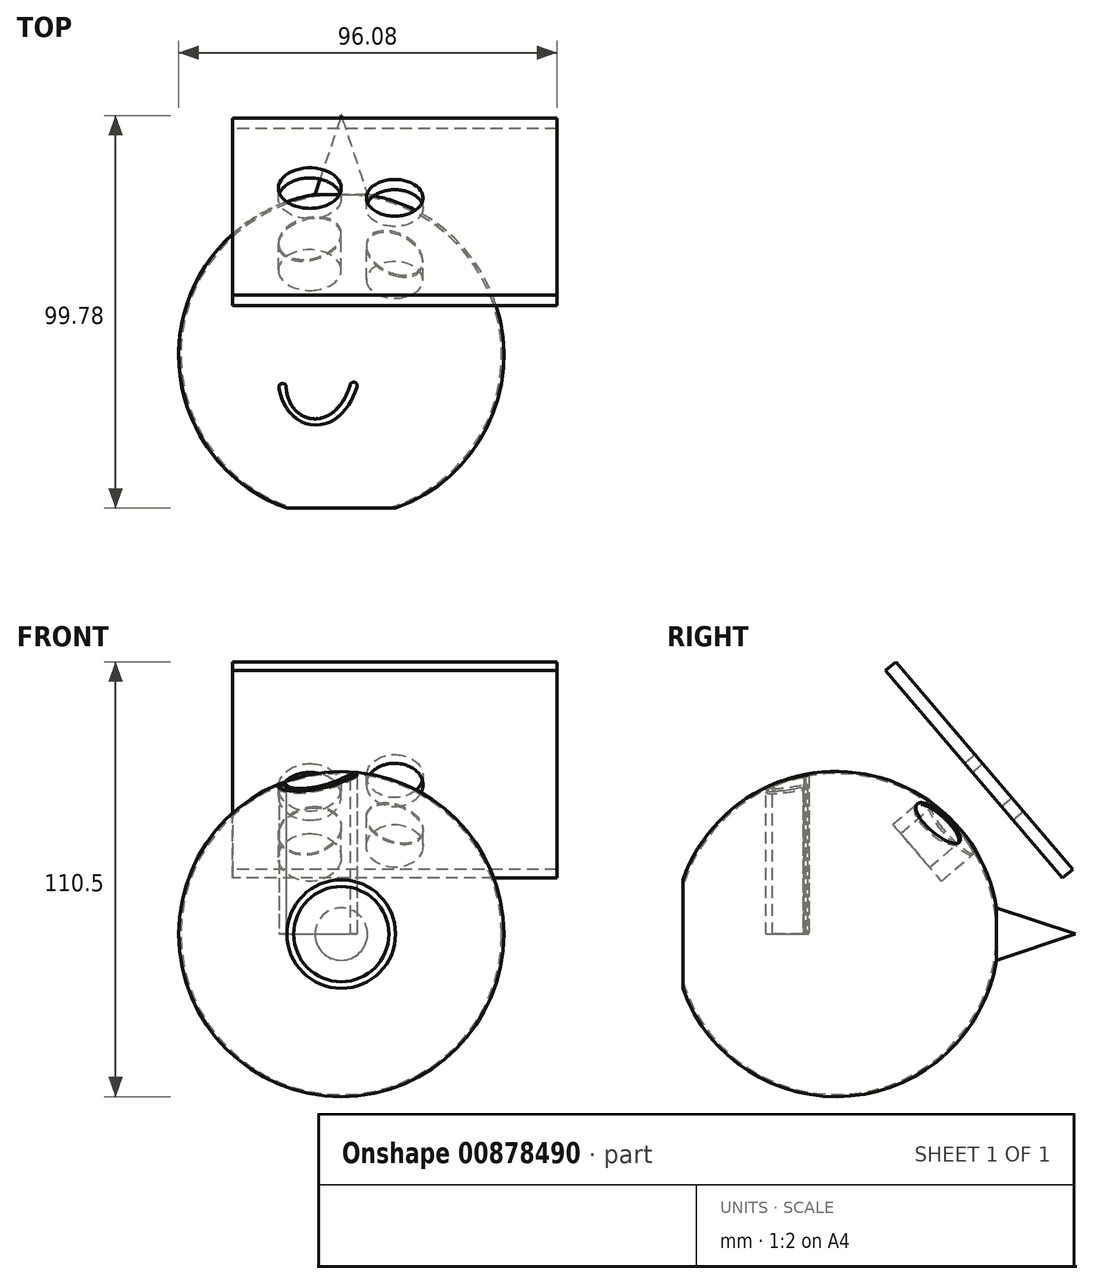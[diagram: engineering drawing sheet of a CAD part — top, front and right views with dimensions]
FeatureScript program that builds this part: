
annotation { "Feature Type Name" : "Feature", "Feature Type Description" : "" }
export const myFeature = defineFeature(function(context is Context, id is Id, definition is map)
    precondition{}
    {
        {
            var Q0;
            Q0=qCreatedBy(makeId("Top.planeOp"),FACE);
            var sketch = newSketch(context, id + "F0", { "sketchPlane" : qUnion([Q0])});
            skLineSegment(sketch, "E0.bottom", {"start": v(-58.97, 67.37) * mm, "end": v(80.08, 67.37) * mm});
            skLineSegment(sketch, "E0.top", {"start": v(-58.97, -42.63) * mm, "end": v(80.08, -42.63) * mm});
            skLineSegment(sketch, "E0.left", {"start": v(-58.97, 67.37) * mm, "end": v(-58.97, -42.63) * mm});
            skLineSegment(sketch, "E0.right", {"start": v(80.08, 67.37) * mm, "end": v(80.08, -42.63) * mm});
            skLineSegment(sketch, "E1", {"start": v(-13.57, 63.6) * mm, "end": v(-13.57, -38.55) * mm});
            skCircle(sketch, "E2", {"center": v(-13.57, 2.76) * mm, "radius": 41.3 * mm});
            skLineSegment(sketch, "E3", {"start": v(-20.22, 43.53) * mm, "end": v(-13.57, 43.53) * mm});
            skCircle(sketch, "E4", {"center": v(-13.57, 2.76) * mm, "radius": 40.77 * mm});
            skLineSegment(sketch, "E5", {"start": v(-20.22, 43.53) * mm, "end": v(-13.57, 63.6) * mm});
            skSolve(sketch);
        }
        {
            var Q0;
            {var subQ0=sQuery(id+"F0.wireOp",EDGE,"E4");var subQ1=sQuery(id+"F0.wireOp",EDGE,"E1");var subQ3=makeQuery(id+"F0.imprint","INTERSECT",VERTEX,{"derivedFrom":[subQ1,subQ0]});Q0=makeQuery(id+"F0.imprint","IMPRINT",FACE,{"disambiguationData":[TD([[makeQuery(id+"F0.imprint","IMPRINT",EDGE,{"disambiguationData":[TD([[subQ3,1.0]])],"derivedFrom":subQ1}),-1.0]])]});}
            var Q1;
            Q1=sQuery(id+"F0.wireOp",EDGE,"E1");
            revolve(context, id + "F1", {"surfaceOperationType" : NewSurfaceOperationType.NEW, "entities" : qUnion([Q0]), "axis" : qUnion([Q1]), "revolveType" : RevolveType.FULL});
        }
        {
            var Q0;
            {var subQ0=sQuery(id+"F0.wireOp",EDGE,"E4");var subQ1=sQuery(id+"F0.wireOp",EDGE,"E1");var subQ3=makeQuery(id+"F0.imprint","INTERSECT",VERTEX,{"derivedFrom":[subQ1,subQ0]});Q0=makeQuery(id+"F0.imprint","IMPRINT",FACE,{"disambiguationData":[TD([[makeQuery(id+"F0.imprint","IMPRINT",EDGE,{"disambiguationData":[TD([[subQ3,1.0]])],"derivedFrom":subQ1}),-1.0]])]});}
            var Q1;
            {var subQ5=sQuery(id+"F0.wireOp",EDGE,"E3");Q1=makeQuery(id+"F0.imprint","IMPRINT",FACE,{"disambiguationData":[TD([[makeQuery(id+"F0.imprint","IMPRINT",EDGE,{"derivedFrom":subQ5}),-1.0]])]});}
            var Q2;
            Q2=sQuery(id+"F0.wireOp",EDGE,"E1");
            revolve(context, id + "F2", {"surfaceOperationType" : NewSurfaceOperationType.NEW, "entities" : qUnion([Q0, Q1]), "axis" : qUnion([Q2]), "revolveType" : RevolveType.FULL});
        }
        {
            var Q0;
            {var subQ0=sQuery(id+"F0.wireOp",EDGE,"E5");Q0=makeQuery(id+"F0.imprint","IMPRINT",FACE,{"disambiguationData":[TD([[makeQuery(id+"F0.imprint","IMPRINT",EDGE,{"derivedFrom":subQ0}),-1.0]])]});}
            var Q1;
            {var subQ0=sQuery(id+"F0.wireOp",EDGE,"E3");Q1=makeQuery(id+"F0.imprint","IMPRINT",FACE,{"disambiguationData":[TD([[makeQuery(id+"F0.imprint","IMPRINT",EDGE,{"derivedFrom":subQ0}),1.0]])]});}
            var Q2;
            Q2=sQuery(id+"F0.wireOp",EDGE,"E1");
            revolve(context, id + "F3", {"surfaceOperationType" : NewSurfaceOperationType.NEW, "entities" : qUnion([Q0, Q1]), "axis" : qUnion([Q2]), "revolveType" : RevolveType.FULL});
        }
        {
            var Q0;
            Q0=qCreatedBy(makeId("Top.planeOp"),FACE);
            var sketch = newSketch(context, id + "F4", { "sketchPlane" : qUnion([Q0])});
            skCircle(sketch, "E6", {"center": v(-28.49, -5.4) * mm, "radius": 0.93 * mm});
            skCircle(sketch, "E7", {"center": v(-10.44, -5.06) * mm, "radius": 0.92 * mm});
            skFitSpline(sketch, "E8", {"points": [v(-27.56, -5.47) * mm, v(-11.36, -5.05) * mm], "startDerivative": vector(1.46, -27.74) * mm, "endDerivative": vector(12.33, 37.63) * mm});
            skFitSpline(sketch, "E9", {"points": [v(-29.39, -5.65) * mm, v(-9.58, -5.4) * mm], "startDerivative": vector(6.27, -34.7) * mm, "endDerivative": vector(13.88, 41.5) * mm});
            skEllipse(sketch, "E10", {"center": v(-5.05, 29.7) * mm, "majorRadius": 5.78 * mm, "minorRadius": 4.59 * mm, "majorAxis": v(-1, 0)});
            skEllipse(sketch, "E11", {"center": v(-25.22, 29.92) * mm, "majorRadius": 6.11 * mm, "minorRadius": 4.51 * mm, "majorAxis": v(1, 0)});
            skSolve(sketch);
        }
        {
            var Q0;
            {var subQ0=sQuery(id+"F4.wireOp",EDGE,"E6");var subQ1=makeQuery(id+"F4.imprint","INTERSECT",VERTEX,{"derivedFrom":[subQ0,sQuery(id+"F4.wireOp",EDGE,"E8")]});Q0=makeQuery(id+"F4.imprint","IMPRINT",FACE,{"disambiguationData":[TD([[makeQuery(id+"F4.imprint","IMPRINT",EDGE,{"disambiguationData":[TD([[subQ1,1.0]])],"derivedFrom":subQ0}),1.0]])]});}
            var Q1;
            {var subQ0=sQuery(id+"F4.wireOp",EDGE,"E8");Q1=makeQuery(id+"F4.imprint","IMPRINT",FACE,{"disambiguationData":[TD([[makeQuery(id+"F4.imprint","IMPRINT",EDGE,{"derivedFrom":subQ0}),-1.0]])]});}
            var Q2;
            {var subQ0=sQuery(id+"F4.wireOp",EDGE,"E7");var subQ1=makeQuery(id+"F4.imprint","INTERSECT",VERTEX,{"derivedFrom":[subQ0,sQuery(id+"F4.wireOp",EDGE,"E8")]});Q2=makeQuery(id+"F4.imprint","IMPRINT",FACE,{"disambiguationData":[TD([[makeQuery(id+"F4.imprint","IMPRINT",EDGE,{"disambiguationData":[TD([[subQ1,-1.0]])],"derivedFrom":subQ0}),1.0]])]});}
            extrude(context, id + "F5", {"entities" : qUnion([Q0, Q1, Q2]), "operationType" : NewBodyOperationType.REMOVE, "depth" : 70.5 * mm, "offsetDistance" : 25 * mm});
        }
        {
            var Q0;
            Q0=qCreatedBy(makeId("Right.planeOp"),FACE);
            var sketch = newSketch(context, id + "F6", { "sketchPlane" : qUnion([Q0])});
            skLineSegment(sketch, "E12", {"start": v(60.22, 14.28) * mm, "end": v(15.34, 66.96) * mm});
            skLineSegment(sketch, "E13", {"start": v(15.34, 66.96) * mm, "end": v(17.96, 69.19) * mm});
            skLineSegment(sketch, "E14", {"start": v(17.96, 69.19) * mm, "end": v(62.92, 16.41) * mm});
            skLineSegment(sketch, "E15", {"start": v(62.92, 16.41) * mm, "end": v(60.22, 14.28) * mm});
            skSolve(sketch);
        }
        {
            var Q0;
            Q0=makeQuery(id+"F6.imprint","IMPRINT",FACE,{"disambiguationData":[TD([[makeQuery(id+"F6.imprint","IMPRINT",EDGE,{"derivedFrom":sQuery(id+"F6.wireOp",EDGE,"E12")}),-1.0]])]});
            extrude(context, id + "F7", {"entities" : qUnion([Q0]), "endBound" : BoundingType.SYMMETRIC, "depth" : 82.4 * mm, "offsetDistance" : 25 * mm});
        }
        {
            var Q0;
            Q0=makeQuery(id+"F7.opExtrude","SWEPT_FACE",FACE,{"disambiguationData":[OSD([sQuery(id+"F6.wireOp",EDGE,"E14")])]});
            var sketch = newSketch(context, id + "F8", { "sketchPlane" : qUnion([Q0])});
            skCircle(sketch, "E16", {"center": v(21.55, -0.95) * mm, "radius": 7.97 * mm});
            skCircle(sketch, "E17", {"center": v(0, 2.87) * mm, "radius": 7.19 * mm});
            skSolve(sketch);
        }
        {
            var Q0;
            Q0=makeQuery(id+"F8.imprint","IMPRINT",FACE,{"disambiguationData":[TD([[makeQuery(id+"F8.imprint","IMPRINT",EDGE,{"derivedFrom":sQuery(id+"F8.wireOp",EDGE,"E16")}),1.0]])]});
            var Q1;
            Q1=makeQuery(id+"F8.imprint","IMPRINT",FACE,{"disambiguationData":[TD([[makeQuery(id+"F8.imprint","IMPRINT",EDGE,{"derivedFrom":sQuery(id+"F8.wireOp",EDGE,"E17")}),1.0]])]});
            extrude(context, id + "F9", {"entities" : qUnion([Q0, Q1]), "operationType" : NewBodyOperationType.REMOVE, "oppositeDirection" : true, "depth" : 27.4 * mm, "offsetDistance" : 25 * mm});
        }
        {
            var Q0;
            Q0=qCreatedBy(makeId("Top.planeOp"),FACE);
            var sketch = newSketch(context, id + "F10", { "sketchPlane" : qUnion([Q0])});
            skLineSegment(sketch, "E18.bottom", {"start": v(-33.49, -36.18) * mm, "end": v(9.49, -36.18) * mm});
            skLineSegment(sketch, "E18.top", {"start": v(-33.49, -41.6) * mm, "end": v(9.49, -41.6) * mm});
            skLineSegment(sketch, "E18.left", {"start": v(-33.49, -36.18) * mm, "end": v(-33.49, -41.6) * mm});
            skLineSegment(sketch, "E18.right", {"start": v(9.49, -36.18) * mm, "end": v(9.49, -41.6) * mm});
            skSolve(sketch);
        }
        {
            var Q0;
            Q0=makeQuery(id+"F10.imprint","IMPRINT",FACE,{"disambiguationData":[TD([[makeQuery(id+"F10.imprint","IMPRINT",EDGE,{"derivedFrom":sQuery(id+"F10.wireOp",EDGE,"E18.bottom")}),-1.0]])]});
            extrude(context, id + "F11", {"entities" : qUnion([Q0]), "operationType" : NewBodyOperationType.REMOVE, "endBound" : BoundingType.SYMMETRIC, "oppositeDirection" : true, "depth" : 47.8 * mm, "offsetDistance" : 25 * mm});
        }
    });
